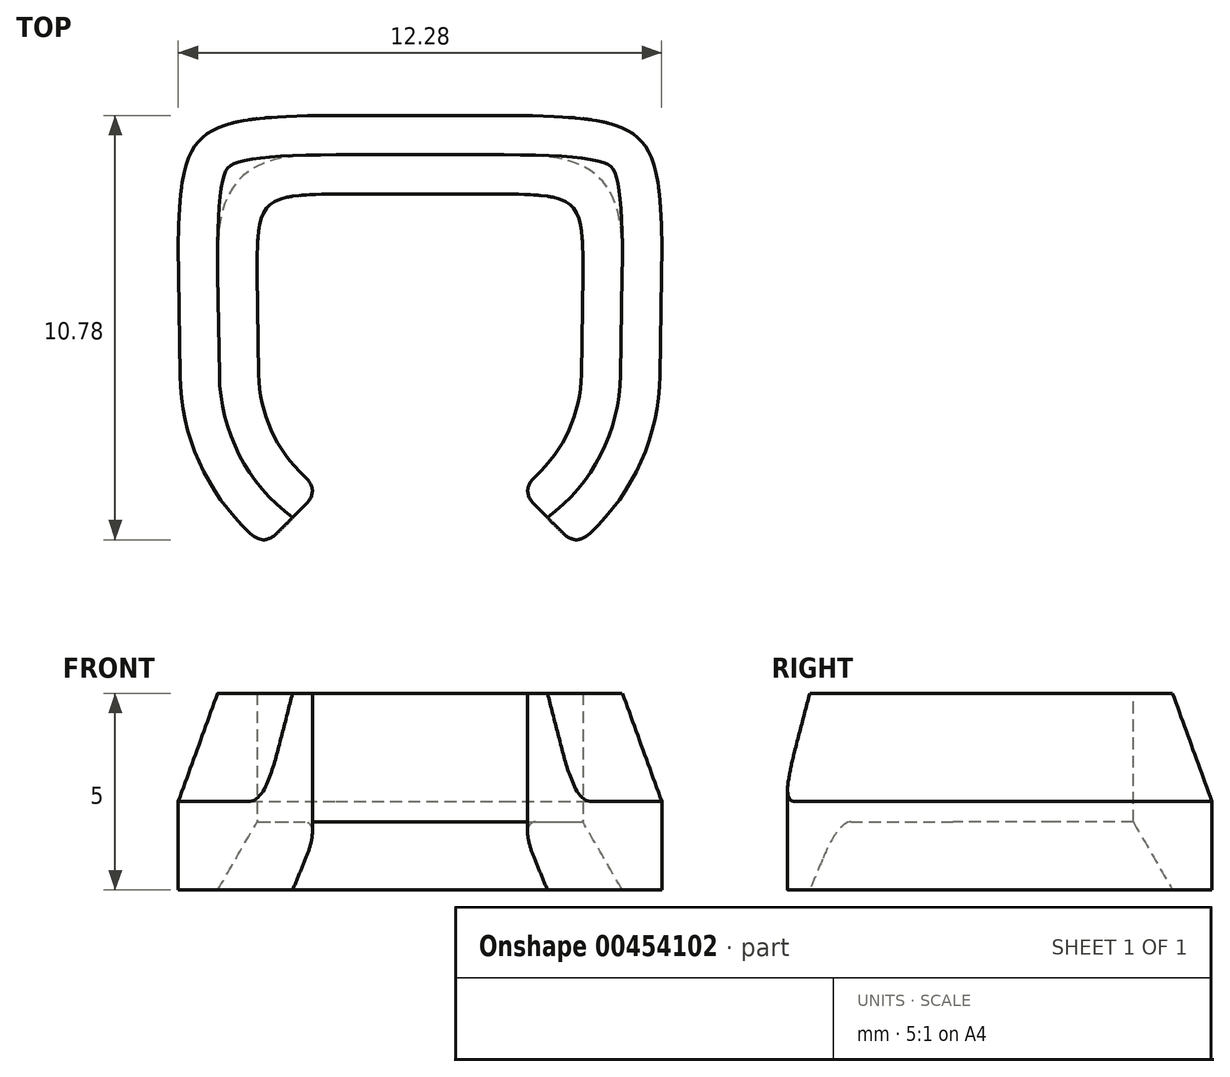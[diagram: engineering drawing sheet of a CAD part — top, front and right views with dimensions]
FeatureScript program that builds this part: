
annotation { "Feature Type Name" : "Feature", "Feature Type Description" : "" }
export const myFeature = defineFeature(function(context is Context, id is Id, definition is map)
    precondition{}
    {
        {
            var Q0;
            Q0=qCreatedBy(makeId("Top.planeOp"),FACE);
            var sketch = newSketch(context, id + "F0", { "sketchPlane" : qUnion([Q0])});
            skLineSegment(sketch, "E0", {"start": v(0, 0) * mm, "end": v(7.15, 0) * mm});
            skLineSegment(sketch, "E1", {"start": v(7.15, 0) * mm, "end": v(7.15, -3) * mm});
            skArc(sketch, "E2", {"start": v(8.15, -9.67) * mm, "mid": v(9.96, -5.99) * mm, "end": v(7.15, -3) * mm});
            skLineSegment(sketch, "E3", {"start": v(7.15, -3) * mm, "end": v(0, -3) * mm, "construction": true});
            skLineSegment(sketch, "E4", {"start": v(10, -6.52) * mm, "end": v(10, 0) * mm, "construction": true});
            skLineSegment(sketch, "E5", {"start": v(10, 0) * mm, "end": v(7.15, 0) * mm, "construction": true});
            skSolve(sketch);
        }
        {
            var Q0;
            Q0=qCreatedBy(makeId("Top.planeOp"),FACE);
            var sketch = newSketch(context, id + "F1", { "sketchPlane" : qUnion([Q0])});
            skArc(sketch, "E6", {"start": v(-54.7, 8.13) * mm, "mid": v(0, -13.5) * mm, "end": v(54.7, 8.13) * mm});
            skLineSegment(sketch, "E7", {"start": v(0, 66.5) * mm, "end": v(0, 0) * mm, "construction": true});
            skLineSegment(sketch, "E8", {"start": v(0, 0) * mm, "end": v(0, -13.5) * mm, "construction": true});
            skArc(sketch, "E9", {"start": v(-43.93, 4.75) * mm, "mid": v(0, -13.5) * mm, "end": v(43.93, 4.75) * mm, "construction": true});
            skSolve(sketch);
        }
        {
            var Q0;
            Q0=qCreatedBy(makeId("Top.planeOp"),FACE);
            var sketch = newSketch(context, id + "F2", { "sketchPlane" : qUnion([Q0])});
            skLineSegment(sketch, "E10", {"start": v(5.5, -2) * mm, "end": v(5.5, 0) * mm});
            skLineSegment(sketch, "E11", {"start": v(5.5, 0) * mm, "end": v(11.7, 0) * mm});
            skLineSegment(sketch, "E12", {"start": v(9.45, -10.93) * mm, "end": v(8.02, -9.5) * mm});
            skLineSegment(sketch, "E13", {"start": v(5.5, -2) * mm, "end": v(9.67, -2) * mm});
            skLineSegment(sketch, "E14", {"start": v(9.67, -2) * mm, "end": v(9.6, -6.58) * mm});
            skArc(sketch, "E15", {"start": v(8.02, -9.5) * mm, "mid": v(9.17, -8.23) * mm, "end": v(9.6, -6.58) * mm});
            skLineSegment(sketch, "E16", {"start": v(11.7, 0) * mm, "end": v(11.6, -6.6) * mm});
            skArc(sketch, "E17", {"start": v(9.45, -10.93) * mm, "mid": v(11.02, -9.01) * mm, "end": v(11.6, -6.6) * mm});
            skSolve(sketch);
        }
        {
            var Q0;
            Q0=qSketchRegion(id+"F2",true);
            extrude(context, id + "F3", {"entities" : qUnion([Q0]), "depth" : 5 * mm});
        }
        {
            var Q0;
            Q0=makeQuery(id+"F3.opExtrude","SWEPT_EDGE",EDGE,{"disambiguationData":[OSD([sQuery(id+"F2.wireOp",EDGE,"E13"),sQuery(id+"F2.wireOp",EDGE,"E14")])]});
            fillet(context, id + "F4", {"entities" : qUnion([Q0]), "radius" : 2 * mm, "tangentPropagation" : true, "rho" : .7, "crossSection" : FilletCrossSection.CONIC, "allowEdgeOverflow" : false});
        }
        {
            var Q0;
            Q0=makeQuery(id+"F3.opExtrude","SWEPT_EDGE",EDGE,{"disambiguationData":[OSD([sQuery(id+"F2.wireOp",EDGE,"E11"),sQuery(id+"F2.wireOp",EDGE,"E16")])]});
            fillet(context, id + "F5", {"entities" : qUnion([Q0]), "radius" : 4 * mm, "tangentPropagation" : true, "rho" : .7, "crossSection" : FilletCrossSection.CONIC, "allowEdgeOverflow" : false});
        }
        {
            var Q0;
            Q0=makeQuery(id+"F3.opExtrude","SWEPT_EDGE",EDGE,{"disambiguationData":[OSD([sQuery(id+"F2.wireOp",EDGE,"E12"),sQuery(id+"F2.wireOp",EDGE,"E15")])]});
            var Q1;
            Q1=makeQuery(id+"F3.opExtrude","SWEPT_EDGE",EDGE,{"disambiguationData":[OSD([sQuery(id+"F2.wireOp",EDGE,"E12"),sQuery(id+"F2.wireOp",EDGE,"E17")])]});
            fillet(context, id + "F6", {"entities" : qUnion([Q0, Q1]), "radius" : .5 * mm, "tangentPropagation" : true, "rho" : .5, "crossSection" : FilletCrossSection.CONIC, "allowEdgeOverflow" : false});
        }
        {
            var Q0;
            Q0=makeQuery(id+"F3.opExtrude","SWEPT_BODY",BODY,{"disambiguationData":[OSD([sQuery(id+"F2.wireOp",EDGE,"E10"),sQuery(id+"F2.wireOp",EDGE,"E11"),sQuery(id+"F2.wireOp",EDGE,"E12"),sQuery(id+"F2.wireOp",EDGE,"E13"),sQuery(id+"F2.wireOp",EDGE,"E14"),sQuery(id+"F2.wireOp",EDGE,"E15"),sQuery(id+"F2.wireOp",EDGE,"E16"),sQuery(id+"F2.wireOp",EDGE,"E17")])]});
            var Q1;
            Q1=makeQuery(id+"FEYfMAQslLhMSq6_1.boolean.opBoolean","MERGE",FACE,{"derivedFrom":[makeQuery(id+"F3.opExtrude","SWEPT_FACE",FACE,{"disambiguationData":[OSD([sQuery(id+"F2.wireOp",EDGE,"E10")])]}),makeQuery(id+"FEYfMAQslLhMSq6_1.opExtrude","SWEPT_FACE",FACE,{"disambiguationData":[OSD([sQuery(id+"FRwAHZ7cPLAG5hV_1.wireOp",EDGE,"NwUQ8mfG-HIWr-BZwG-7fB6-xsCqPSEjDOeQ.left")])]})]});
            mirror(context, id + "F7", {"operationType" : NewBodyOperationType.ADD, "entities" : qUnion([Q0]), "mirrorPlane" : qUnion([Q1])});
        }
        {
            var Q0;
            {var subQ0=makeQuery(id+"F3.opExtrude","CAP_EDGE",EDGE,{"disambiguationData":[OSD([sQuery(id+"F2.wireOp",EDGE,"E11")])],"isStart":false});Q0=makeQuery(id+"F7.boolean.opBoolean","MERGE",EDGE,{"derivedFrom":[subQ0,makeQuery(id+"F7.opPattern","COPY",EDGE,{"derivedFrom":subQ0,"instanceName":"1"})]});}
            var Q1;
            {var subQ0=sQuery(id+"F2.wireOp",EDGE,"E16");var subQ1=sQuery(id+"F2.wireOp",EDGE,"E11");Q1=makeQuery(id+"F5.opFillet","BLEND_EDGE",EDGE,{"blendedFrom":[makeQuery(id+"F3.opExtrude","SWEPT_EDGE",EDGE,{"disambiguationData":[OSD([subQ1,subQ0])]}),makeQuery(id+"F3.opExtrude","CAP_FACE",FACE,{"disambiguationData":[OSD([sQuery(id+"F2.wireOp",EDGE,"E10"),subQ1,sQuery(id+"F2.wireOp",EDGE,"E12"),sQuery(id+"F2.wireOp",EDGE,"E13"),sQuery(id+"F2.wireOp",EDGE,"E14"),sQuery(id+"F2.wireOp",EDGE,"E15"),subQ0,sQuery(id+"F2.wireOp",EDGE,"E17")])],"isStart":false})],"blendedInto":[makeQuery(id+"F3.opExtrude","CAP_FACE",FACE,{"disambiguationData":[OSD([sQuery(id+"F2.wireOp",EDGE,"E10"),subQ1,sQuery(id+"F2.wireOp",EDGE,"E12"),sQuery(id+"F2.wireOp",EDGE,"E13"),sQuery(id+"F2.wireOp",EDGE,"E14"),sQuery(id+"F2.wireOp",EDGE,"E15"),subQ0,sQuery(id+"F2.wireOp",EDGE,"E17")])],"isStart":false})]});}
            var Q2;
            {var subQ0=sQuery(id+"F2.wireOp",EDGE,"E16");var subQ1=sQuery(id+"F2.wireOp",EDGE,"E11");Q2=makeQuery(id+"F7.opPattern","COPY",EDGE,{"derivedFrom":makeQuery(id+"F5.opFillet","BLEND_EDGE",EDGE,{"blendedFrom":[makeQuery(id+"F3.opExtrude","SWEPT_EDGE",EDGE,{"disambiguationData":[OSD([subQ1,subQ0])]}),makeQuery(id+"F3.opExtrude","CAP_FACE",FACE,{"disambiguationData":[OSD([sQuery(id+"F2.wireOp",EDGE,"E10"),subQ1,sQuery(id+"F2.wireOp",EDGE,"E12"),sQuery(id+"F2.wireOp",EDGE,"E13"),sQuery(id+"F2.wireOp",EDGE,"E14"),sQuery(id+"F2.wireOp",EDGE,"E15"),subQ0,sQuery(id+"F2.wireOp",EDGE,"E17")])],"isStart":false})],"blendedInto":[makeQuery(id+"F3.opExtrude","CAP_FACE",FACE,{"disambiguationData":[OSD([sQuery(id+"F2.wireOp",EDGE,"E10"),subQ1,sQuery(id+"F2.wireOp",EDGE,"E12"),sQuery(id+"F2.wireOp",EDGE,"E13"),sQuery(id+"F2.wireOp",EDGE,"E14"),sQuery(id+"F2.wireOp",EDGE,"E15"),subQ0,sQuery(id+"F2.wireOp",EDGE,"E17")])],"isStart":false})]}),"instanceName":"1"});}
            var Q3;
            Q3=makeQuery(id+"F7.opPattern","COPY",EDGE,{"derivedFrom":makeQuery(id+"F3.opExtrude","CAP_EDGE",EDGE,{"disambiguationData":[OSD([sQuery(id+"F2.wireOp",EDGE,"E16")])],"isStart":false}),"instanceName":"1"});
            var Q4;
            Q4=makeQuery(id+"F7.opPattern","COPY",EDGE,{"derivedFrom":makeQuery(id+"F3.opExtrude","CAP_EDGE",EDGE,{"disambiguationData":[OSD([sQuery(id+"F2.wireOp",EDGE,"E17")])],"isStart":false}),"instanceName":"1"});
            var Q5;
            Q5=makeQuery(id+"F3.opExtrude","CAP_EDGE",EDGE,{"disambiguationData":[OSD([sQuery(id+"F2.wireOp",EDGE,"E17")])],"isStart":false});
            chamfer(context, id + "F8", {"entities" : qUnion([Q0, Q1, Q2, Q3, Q4, Q5]), "chamferType" : ChamferType.OFFSET_ANGLE, "width" : 1 * mm, "oppositeDirection" : true, "angle" : 70 * degree});
        }
        {
            var Q0;
            {var subQ0=makeQuery(id+"F3.opExtrude","CAP_EDGE",EDGE,{"disambiguationData":[OSD([sQuery(id+"F2.wireOp",EDGE,"E13")])],"isStart":true});Q0=makeQuery(id+"F7.boolean.opBoolean","MERGE",EDGE,{"derivedFrom":[subQ0,makeQuery(id+"F7.opPattern","COPY",EDGE,{"derivedFrom":subQ0,"instanceName":"1"})]});}
            var Q1;
            {var subQ0=sQuery(id+"F2.wireOp",EDGE,"E14");var subQ1=sQuery(id+"F2.wireOp",EDGE,"E13");Q1=makeQuery(id+"F4.opFillet","BLEND_EDGE",EDGE,{"blendedFrom":[makeQuery(id+"F3.opExtrude","SWEPT_EDGE",EDGE,{"disambiguationData":[OSD([subQ1,subQ0])]}),makeQuery(id+"F3.opExtrude","CAP_FACE",FACE,{"disambiguationData":[OSD([sQuery(id+"F2.wireOp",EDGE,"E10"),sQuery(id+"F2.wireOp",EDGE,"E11"),sQuery(id+"F2.wireOp",EDGE,"E12"),subQ1,subQ0,sQuery(id+"F2.wireOp",EDGE,"E15"),sQuery(id+"F2.wireOp",EDGE,"E16"),sQuery(id+"F2.wireOp",EDGE,"E17")])],"isStart":true})],"blendedInto":[makeQuery(id+"F3.opExtrude","CAP_FACE",FACE,{"disambiguationData":[OSD([sQuery(id+"F2.wireOp",EDGE,"E10"),sQuery(id+"F2.wireOp",EDGE,"E11"),sQuery(id+"F2.wireOp",EDGE,"E12"),subQ1,subQ0,sQuery(id+"F2.wireOp",EDGE,"E15"),sQuery(id+"F2.wireOp",EDGE,"E16"),sQuery(id+"F2.wireOp",EDGE,"E17")])],"isStart":true})]});}
            var Q2;
            {var subQ0=sQuery(id+"F2.wireOp",EDGE,"E14");var subQ1=sQuery(id+"F2.wireOp",EDGE,"E13");Q2=makeQuery(id+"F7.opPattern","COPY",EDGE,{"derivedFrom":makeQuery(id+"F4.opFillet","BLEND_EDGE",EDGE,{"blendedFrom":[makeQuery(id+"F3.opExtrude","SWEPT_EDGE",EDGE,{"disambiguationData":[OSD([subQ1,subQ0])]}),makeQuery(id+"F3.opExtrude","CAP_FACE",FACE,{"disambiguationData":[OSD([sQuery(id+"F2.wireOp",EDGE,"E10"),sQuery(id+"F2.wireOp",EDGE,"E11"),sQuery(id+"F2.wireOp",EDGE,"E12"),subQ1,subQ0,sQuery(id+"F2.wireOp",EDGE,"E15"),sQuery(id+"F2.wireOp",EDGE,"E16"),sQuery(id+"F2.wireOp",EDGE,"E17")])],"isStart":true})],"blendedInto":[makeQuery(id+"F3.opExtrude","CAP_FACE",FACE,{"disambiguationData":[OSD([sQuery(id+"F2.wireOp",EDGE,"E10"),sQuery(id+"F2.wireOp",EDGE,"E11"),sQuery(id+"F2.wireOp",EDGE,"E12"),subQ1,subQ0,sQuery(id+"F2.wireOp",EDGE,"E15"),sQuery(id+"F2.wireOp",EDGE,"E16"),sQuery(id+"F2.wireOp",EDGE,"E17")])],"isStart":true})]}),"instanceName":"1"});}
            var Q3;
            Q3=makeQuery(id+"F7.opPattern","COPY",EDGE,{"derivedFrom":makeQuery(id+"F3.opExtrude","CAP_EDGE",EDGE,{"disambiguationData":[OSD([sQuery(id+"F2.wireOp",EDGE,"E14")])],"isStart":true}),"instanceName":"1"});
            var Q4;
            Q4=makeQuery(id+"F7.opPattern","COPY",EDGE,{"derivedFrom":makeQuery(id+"F3.opExtrude","CAP_EDGE",EDGE,{"disambiguationData":[OSD([sQuery(id+"F2.wireOp",EDGE,"E15")])],"isStart":true}),"instanceName":"1"});
            var Q5;
            Q5=makeQuery(id+"F3.opExtrude","CAP_EDGE",EDGE,{"disambiguationData":[OSD([sQuery(id+"F2.wireOp",EDGE,"E15")])],"isStart":true});
            var Q6;
            Q6=makeQuery(id+"F3.opExtrude","CAP_EDGE",EDGE,{"disambiguationData":[OSD([sQuery(id+"F2.wireOp",EDGE,"E14")])],"isStart":true});
            chamfer(context, id + "F9", {"entities" : qUnion([Q0, Q1, Q2, Q3, Q4, Q5, Q6]), "chamferType" : ChamferType.OFFSET_ANGLE, "width" : 1 * mm, "oppositeDirection" : true, "angle" : 60 * degree});
        }
    });
